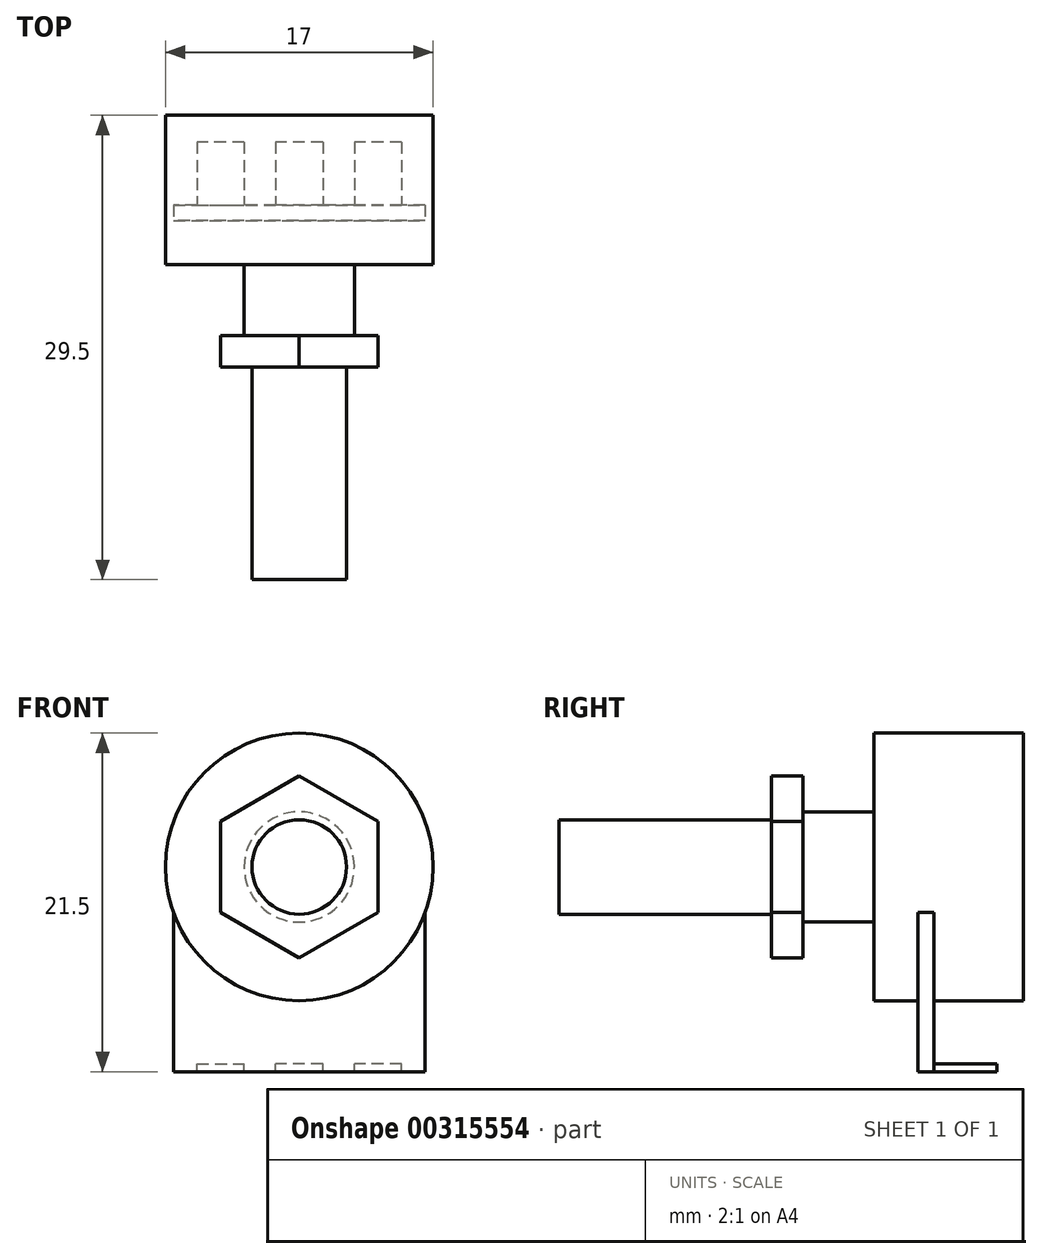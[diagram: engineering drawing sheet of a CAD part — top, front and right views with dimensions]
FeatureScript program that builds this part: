
annotation { "Feature Type Name" : "Feature", "Feature Type Description" : "" }
export const myFeature = defineFeature(function(context is Context, id is Id, definition is map)
    precondition{}
    {
        {
            var Q0;
            Q0=qCreatedBy(makeId("Front.planeOp"),FACE);
            var sketch = newSketch(context, id + "F0", { "sketchPlane" : qUnion([Q0])});
            skCircle(sketch, "E0", {"center": v(0, 0) * mm, "radius": 8.5 * mm});
            skSolve(sketch);
        }
        {
            var Q0;
            Q0 = qSketchRegion(id + "F0", true);
            extrude(context, id + "F1", {"entities" : qUnion([Q0]), "oppositeDirection" : true, "depth" : 9.5 * mm});
        }
        {
            var Q0;
            Q0=qCreatedBy(makeId("Front.planeOp"),FACE);
            cPlane(context, id + "F2", {"entities" : qUnion([Q0]), "cplaneType" : CPlaneType.OFFSET, "offset" : 3.8 * mm, "oppositeDirection" : true, "width" : 150 * mm, "height" : 150 * mm});
        }
        {
            var Q0;
            Q0=qCreatedBy(id+"F2.planeOp",FACE);
            var sketch = newSketch(context, id + "F3", { "sketchPlane" : qUnion([Q0])});
            skLineSegment(sketch, "E1.bottom", {"start": v(8, -13) * mm, "end": v(-8, -13) * mm});
            skLineSegment(sketch, "E1.top", {"start": v(8, 1) * mm, "end": v(-8, 1) * mm});
            skLineSegment(sketch, "E1.left", {"start": v(8, -13) * mm, "end": v(8, 1) * mm});
            skLineSegment(sketch, "E1.right", {"start": v(-8, -13) * mm, "end": v(-8, 1) * mm});
            skPoint(sketch, "E1.middle", {"position": v(0, -6) * mm});
            skSolve(sketch);
        }
        {
            var Q0;
            Q0 = qSketchRegion(id + "F3", true);
            extrude(context, id + "F4", {"entities" : qUnion([Q0]), "operationType" : NewBodyOperationType.ADD, "depth" : 1 * mm});
        }
        {
            var Q0;
            Q0=makeQuery(id+"F4.opExtrude","CAP_FACE",FACE,{"disambiguationData":[OSD([sQuery(id+"F3.wireOp",EDGE,"E1.bottom"),sQuery(id+"F3.wireOp",EDGE,"E1.top"),sQuery(id+"F3.wireOp",EDGE,"E1.left"),sQuery(id+"F3.wireOp",EDGE,"E1.right")])],"isStart":true});
            var sketch = newSketch(context, id + "F5", { "sketchPlane" : qUnion([Q0])});
            skLineSegment(sketch, "E2.bottom", {"start": v(-1.5, -13) * mm, "end": v(1.5, -13) * mm});
            skLineSegment(sketch, "E2.top", {"start": v(-1.5, -12.5) * mm, "end": v(1.5, -12.5) * mm});
            skLineSegment(sketch, "E2.left", {"start": v(-1.5, -13) * mm, "end": v(-1.5, -12.5) * mm});
            skLineSegment(sketch, "E2.right", {"start": v(1.5, -13) * mm, "end": v(1.5, -12.5) * mm});
            skLineSegment(sketch, "E3.bottom", {"start": v(-6.5, -13) * mm, "end": v(-3.5, -13) * mm});
            skLineSegment(sketch, "E3.top", {"start": v(-6.5, -12.5) * mm, "end": v(-3.5, -12.5) * mm});
            skLineSegment(sketch, "E3.left", {"start": v(-6.5, -13) * mm, "end": v(-6.5, -12.5) * mm});
            skLineSegment(sketch, "E3.right", {"start": v(-3.5, -13) * mm, "end": v(-3.5, -12.5) * mm});
            skLineSegment(sketch, "E4", {"start": v(0, -12.5) * mm, "end": v(0, -13) * mm, "construction": true});
            skLineSegment(sketch, "E5.MirrorCS", {"start": v(6.5, -13) * mm, "end": v(3.5, -13) * mm});
            skLineSegment(sketch, "E6.MirrorCS", {"start": v(6.5, -12.5) * mm, "end": v(3.5, -12.5) * mm});
            skLineSegment(sketch, "E7.MirrorCS", {"start": v(6.5, -13) * mm, "end": v(6.5, -12.5) * mm});
            skLineSegment(sketch, "E8.MirrorCS", {"start": v(3.5, -13) * mm, "end": v(3.5, -12.5) * mm});
            skSolve(sketch);
        }
        {
            var Q0;
            Q0 = qSketchRegion(id + "F5", true);
            extrude(context, id + "F6", {"entities" : qUnion([Q0]), "operationType" : NewBodyOperationType.ADD, "depth" : 4 * mm});
        }
        {
            var Q0;
            Q0=makeQuery(id+"F1.opExtrude","CAP_FACE",FACE,{"disambiguationData":[OSD([sQuery(id+"F0.wireOp",EDGE,"E0")])],"isStart":true});
            var sketch = newSketch(context, id + "F7", { "sketchPlane" : qUnion([Q0])});
            skCircle(sketch, "E9", {"center": v(0, 0) * mm, "radius": 3.5 * mm});
            skSolve(sketch);
        }
        {
            var Q0;
            Q0 = qSketchRegion(id + "F7", true);
            extrude(context, id + "F8", {"entities" : qUnion([Q0]), "operationType" : NewBodyOperationType.ADD, "depth" : 6.5 * mm});
        }
        {
            var Q0;
            Q0=makeQuery(id+"F8.opExtrude","CAP_FACE",FACE,{"disambiguationData":[OSD([sQuery(id+"F7.wireOp",EDGE,"E9")])],"isStart":false});
            var sketch = newSketch(context, id + "F9", { "sketchPlane" : qUnion([Q0])});
            skCircle(sketch, "E10", {"center": v(0, 0) * mm, "radius": 3 * mm});
            skSolve(sketch);
        }
        {
            var Q0;
            Q0 = qSketchRegion(id + "F9", true);
            extrude(context, id + "F10", {"entities" : qUnion([Q0]), "operationType" : NewBodyOperationType.ADD, "depth" : 13.5 * mm});
        }
        {
            var Q0;
            Q0=makeQuery(id+"F8.opExtrude","CAP_FACE",FACE,{"disambiguationData":[OSD([sQuery(id+"F7.wireOp",EDGE,"E9")])],"isStart":false});
            var sketch = newSketch(context, id + "F11", { "sketchPlane" : qUnion([Q0])});
            skCircle(sketch, "E11.cCircle", {"center": v(0, 0) * mm, "radius": 5 * mm, "construction": true});
            skLineSegment(sketch, "E11.0", {"start": v(5, 2.89) * mm, "end": v(5, -2.89) * mm});
            skLineSegment(sketch, "E11.1", {"start": v(5, -2.89) * mm, "end": v(0, -5.77) * mm});
            skLineSegment(sketch, "E11.2", {"start": v(0, -5.77) * mm, "end": v(-5, -2.89) * mm});
            skLineSegment(sketch, "E11.3", {"start": v(-5, -2.89) * mm, "end": v(-5, 2.89) * mm});
            skLineSegment(sketch, "E11.4", {"start": v(-5, 2.89) * mm, "end": v(0, 5.77) * mm});
            skLineSegment(sketch, "E11.5", {"start": v(0, 5.77) * mm, "end": v(5, 2.89) * mm});
            skPoint(sketch, "E11.0.midPoint", {"position": v(5, 0) * mm});
            skSolve(sketch);
        }
        {
            var Q0;
            Q0 = qSketchRegion(id + "F11", true);
            extrude(context, id + "F12", {"entities" : qUnion([Q0]), "operationType" : NewBodyOperationType.ADD, "oppositeDirection" : true, "depth" : 2 * mm});
        }
    });
